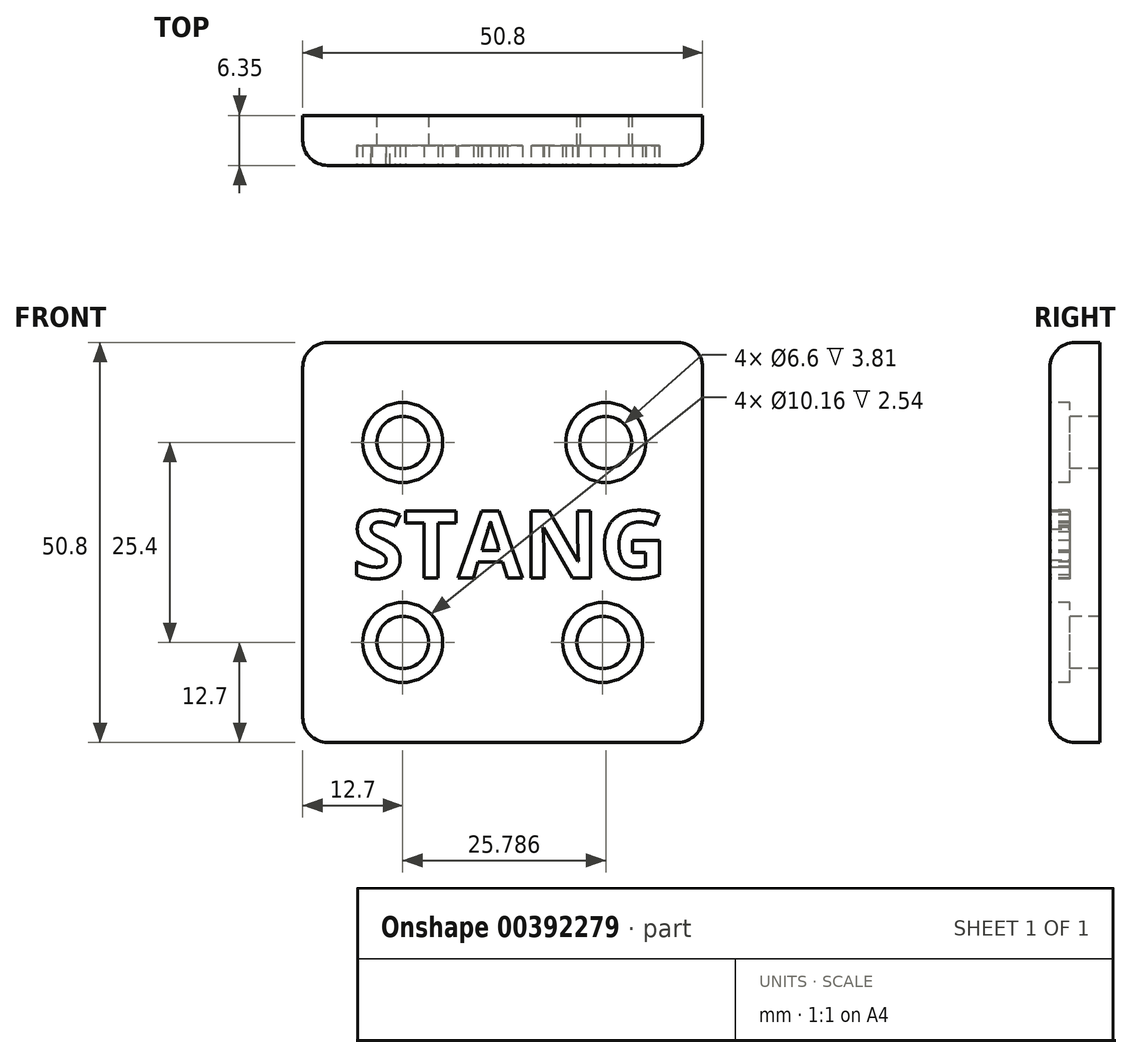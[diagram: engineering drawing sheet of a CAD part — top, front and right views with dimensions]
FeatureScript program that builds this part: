
annotation { "Feature Type Name" : "Feature", "Feature Type Description" : "" }
export const myFeature = defineFeature(function(context is Context, id is Id, definition is map)
    precondition{}
    {
        {
            var Q0;
            Q0=qCreatedBy(makeId("Front.planeOp"),FACE);
            var sketch = newSketch(context, id + "F0", { "sketchPlane" : qUnion([Q0])});
            skLineSegment(sketch, "E0.bottom", {"start": v(25.4, 25.4) * mm, "end": v(-25.4, 25.4) * mm});
            skLineSegment(sketch, "E0.top", {"start": v(25.4, -25.4) * mm, "end": v(-25.4, -25.4) * mm});
            skLineSegment(sketch, "E0.left", {"start": v(25.4, 25.4) * mm, "end": v(25.4, -25.4) * mm});
            skLineSegment(sketch, "E0.right", {"start": v(-25.4, 25.4) * mm, "end": v(-25.4, -25.4) * mm});
            skPoint(sketch, "E0.middle", {"position": v(0, 0) * mm});
            skSolve(sketch);
        }
        {
            var Q0;
            Q0=qCreatedBy(makeId("Front.planeOp"),FACE);
            var sketch = newSketch(context, id + "F1", { "sketchPlane" : qUnion([Q0])});
            skCircle(sketch, "E1", {"center": v(-12.7, -12.7) * mm, "radius": 3.18 * mm});
            skCircle(sketch, "E2", {"center": v(12.7, -12.7) * mm, "radius": 3.18 * mm});
            skCircle(sketch, "E3", {"center": v(-12.7, 12.7) * mm, "radius": 3.18 * mm});
            skCircle(sketch, "E4", {"center": v(13.09, 12.7) * mm, "radius": 3.18 * mm});
            skSolve(sketch);
        }
        {
            var Q0;
            Q0=makeQuery(id+"F0.imprint","IMPRINT",FACE,{"disambiguationData":[TD([[makeQuery(id+"F0.imprint","IMPRINT",EDGE,{"derivedFrom":sQuery(id+"F0.wireOp",EDGE,"E0.bottom")}),1.0]])]});
            extrude(context, id + "F2", {"entities" : qUnion([Q0]), "oppositeDirection" : true, "depth" : 6.35 * mm});
        }
        {
            var Q0;
            Q0=sQuery(id+"F1.wireOp",VERTEX,"E3.center");
            var Q1;
            Q1=sQuery(id+"F1.wireOp",VERTEX,"E4.center");
            var Q2;
            Q2=sQuery(id+"F1.wireOp",VERTEX,"E2.center");
            var Q3;
            Q3=sQuery(id+"F1.wireOp",VERTEX,"E1.center");
            var Q4;
            Q4=makeQuery(id+"F2.opExtrude","SWEPT_BODY",BODY,{"disambiguationData":[OSD([sQuery(id+"F0.wireOp",EDGE,"E0.bottom"),sQuery(id+"F0.wireOp",EDGE,"E0.top"),sQuery(id+"F0.wireOp",EDGE,"E0.left"),sQuery(id+"F0.wireOp",EDGE,"E0.right")])]});
            hole(context, id + "F3", {"style" : HoleStyle.C_BORE, "endStyle" : HoleEndStyle.THROUGH, "holeDiameter" : 6.6 * mm, "cBoreDiameter" : 10.16 * mm, "cBoreDepth" : 2.54 * mm, "isTappedThrough" : true, "tappedDepth" : 12.7 * mm, "tapClearance" : 3, "locations" : qUnion([Q0, Q1, Q2, Q3]), "scope" : qUnion([Q4])});
        }
        {
            var Q0;
            Q0=makeQuery(id+"F2.opExtrude","SWEPT_EDGE",EDGE,{"disambiguationData":[OSD([sQuery(id+"F0.wireOp",EDGE,"E0.bottom"),sQuery(id+"F0.wireOp",EDGE,"E0.left")])]});
            var Q1;
            Q1=makeQuery(id+"F2.opExtrude","SWEPT_EDGE",EDGE,{"disambiguationData":[OSD([sQuery(id+"F0.wireOp",EDGE,"E0.top"),sQuery(id+"F0.wireOp",EDGE,"E0.left")])]});
            var Q2;
            Q2=makeQuery(id+"F2.opExtrude","SWEPT_EDGE",EDGE,{"disambiguationData":[OSD([sQuery(id+"F0.wireOp",EDGE,"E0.top"),sQuery(id+"F0.wireOp",EDGE,"E0.right")])]});
            var Q3;
            Q3=makeQuery(id+"F2.opExtrude","SWEPT_EDGE",EDGE,{"disambiguationData":[OSD([sQuery(id+"F0.wireOp",EDGE,"E0.bottom"),sQuery(id+"F0.wireOp",EDGE,"E0.right")])]});
            fillet(context, id + "F4", {"entities" : qUnion([Q0, Q1, Q2, Q3]), "radius" : 3.17 * mm, "tangentPropagation" : true, "allowEdgeOverflow" : false});
        }
        {
            var Q0;
            Q0=makeQuery(id+"F2.opExtrude","CAP_EDGE",EDGE,{"disambiguationData":[OSD([sQuery(id+"F0.wireOp",EDGE,"E0.bottom")])],"isStart":true});
            fillet(context, id + "F5", {"entities" : qUnion([Q0]), "radius" : 3.17 * mm, "tangentPropagation" : true, "allowEdgeOverflow" : false});
        }
        {
            var Q0;
            Q0=qCreatedBy(makeId("Front.planeOp"),FACE);
            var sketch = newSketch(context, id + "F6", { "sketchPlane" : qUnion([Q0])});
            skText(sketch, "E5", { "text": "STANG", "fontName": "OpenSans-Bold.ttf"});
            const initialGuessF6  = {"E5": [-0.01912, -0.00452, 1, 0, 0.00857]};
            skSetInitialGuess(sketch, initialGuessF6);
            skSolve(sketch);
        }
        {
            var Q0;
            Q0 = qSketchRegion(id + "F6", true);
            extrude(context, id + "F7", {"entities" : qUnion([Q0]), "operationType" : NewBodyOperationType.REMOVE, "oppositeDirection" : true, "depth" : 2.54 * mm});
        }
    });
